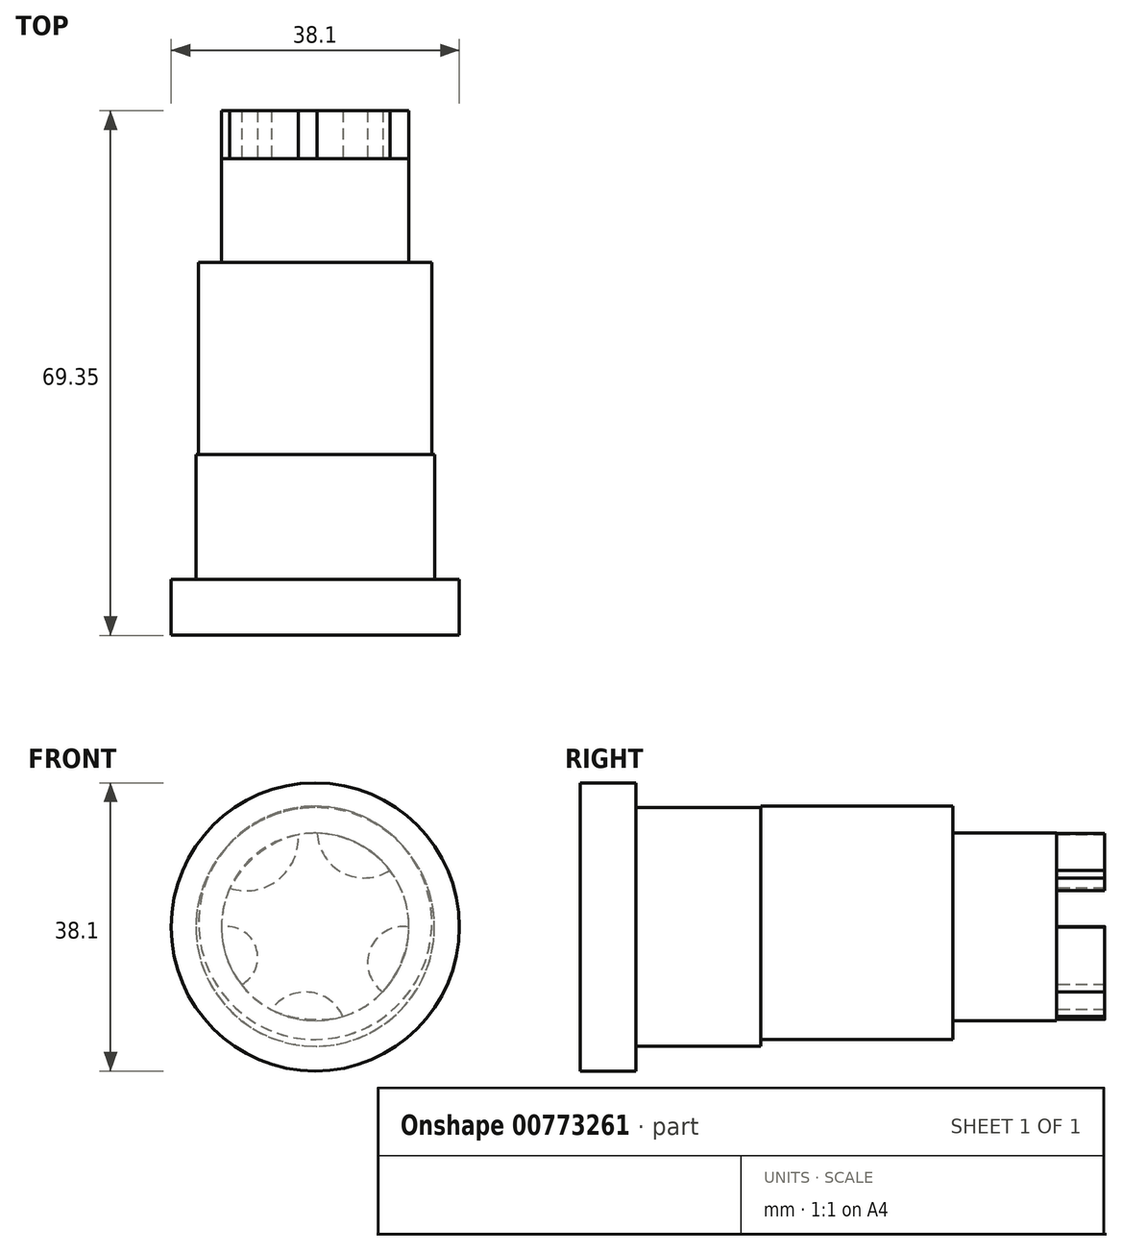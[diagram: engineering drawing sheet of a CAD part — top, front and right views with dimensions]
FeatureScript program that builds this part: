
annotation { "Feature Type Name" : "Feature", "Feature Type Description" : "" }
export const myFeature = defineFeature(function(context is Context, id is Id, definition is map)
    precondition{}
    {
        {
            var Q0;
            Q0=qCreatedBy(makeId("Front.planeOp"),FACE);
            var sketch = newSketch(context, id + "F0", { "sketchPlane" : qUnion([Q0])});
            skCircle(sketch, "E0", {"center": v(0, 0) * mm, "radius": 19.05 * mm});
            skSolve(sketch);
        }
        {
            var Q0;
            Q0 = qSketchRegion(id + "F0", true);
            extrude(context, id + "F1", {"entities" : qUnion([Q0]), "depth" : 7.37 * mm, "offsetDistance" : 25.4 * mm});
        }
        {
            var Q0;
            Q0=makeQuery(id+"F1.opExtrude","CAP_FACE",FACE,{"disambiguationData":[OSD([sQuery(id+"F0.wireOp",EDGE,"E0")])],"isStart":true});
            var sketch = newSketch(context, id + "F2", { "sketchPlane" : qUnion([Q0])});
            skCircle(sketch, "E1", {"center": v(0, 0) * mm, "radius": 15.77 * mm});
            skSolve(sketch);
        }
        {
            var Q0;
            Q0 = qSketchRegion(id + "F2", true);
            extrude(context, id + "F3", {"entities" : qUnion([Q0]), "operationType" : NewBodyOperationType.ADD, "depth" : 16.5 * mm, "offsetDistance" : 25.4 * mm});
        }
        {
            var Q0;
            Q0=makeQuery(id+"F3.opExtrude","CAP_FACE",FACE,{"disambiguationData":[OSD([sQuery(id+"F2.wireOp",EDGE,"E1")])],"isStart":false});
            var sketch = newSketch(context, id + "F4", { "sketchPlane" : qUnion([Q0])});
            skCircle(sketch, "E2", {"center": v(0, 0.54) * mm, "radius": 15.42 * mm});
            skSolve(sketch);
        }
        {
            var Q0;
            Q0 = qSketchRegion(id + "F4", true);
            extrude(context, id + "F5", {"entities" : qUnion([Q0]), "operationType" : NewBodyOperationType.ADD, "depth" : 25.4 * mm, "offsetDistance" : 25.4 * mm});
        }
        {
            var Q0;
            Q0=makeQuery(id+"F5.opExtrude","CAP_FACE",FACE,{"disambiguationData":[OSD([sQuery(id+"F4.wireOp",EDGE,"E2")])],"isStart":false});
            var sketch = newSketch(context, id + "F6", { "sketchPlane" : qUnion([Q0])});
            skCircle(sketch, "E3", {"center": v(0, 0) * mm, "radius": 10.8 * mm});
            skSolve(sketch);
        }
        {
            var Q0;
            Q0=makeQuery(id+"F6.imprint","IMPRINT",FACE,{"disambiguationData":[TD([[makeQuery(id+"F6.imprint","IMPRINT",EDGE,{"derivedFrom":sQuery(id+"F6.wireOp",EDGE,"E3")}),-1.0]])]});
            var sketch = newSketch(context, id + "F7", { "sketchPlane" : qUnion([Q0])});
            skCircle(sketch, "E4", {"center": v(0, 0) * mm, "radius": 12.4 * mm});
            skSolve(sketch);
        }
        {
            var Q0;
            Q0 = qSketchRegion(id + "F7", true);
            extrude(context, id + "F8", {"entities" : qUnion([Q0]), "operationType" : NewBodyOperationType.ADD, "depth" : 13.72 * mm, "offsetDistance" : 25.4 * mm});
        }
        {
            var Q0;
            Q0=makeQuery(id+"F8.opExtrude","CAP_FACE",FACE,{"disambiguationData":[OSD([sQuery(id+"F7.wireOp",EDGE,"E4")])],"isStart":false});
            var sketch = newSketch(context, id + "F9", { "sketchPlane" : qUnion([Q0])});
            skArc(sketch, "E5", {"start": v(-3.67, -11.83) * mm, "mid": v(1.14, -12.17) * mm, "end": v(5.81, -10.94) * mm});
            skArc(sketch, "E6", {"start": v(9.76, -7.63) * mm, "mid": v(11.73, -4.04) * mm, "end": v(12.4, 0) * mm});
            skArc(sketch, "E7", {"start": v(11.28, 5.12) * mm, "mid": v(7.56, 9.65) * mm, "end": v(2.27, 12.18) * mm});
            skArc(sketch, "E8", {"start": v(-12.4, 0) * mm, "mid": v(-11.43, -4.6) * mm, "end": v(-8.93, -8.59) * mm});
            skArc(sketch, "E9", {"start": v(-0.24, 12.39) * mm, "mid": v(-5.6, 11) * mm, "end": v(-9.88, 7.48) * mm});
            skArc(sketch, "E10", {"start": v(5.81, -10.94) * mm, "mid": v(0.81, -8.64) * mm, "end": v(-3.67, -11.83) * mm});
            skArc(sketch, "E11", {"start": v(12.4, 0) * mm, "mid": v(7.83, -2.7) * mm, "end": v(9.76, -7.63) * mm});
            skArc(sketch, "E12", {"start": v(2.27, 12.18) * mm, "mid": v(4.9, 6.25) * mm, "end": v(11.28, 5.12) * mm});
            skArc(sketch, "E13", {"start": v(-9.88, 7.48) * mm, "mid": v(-3.65, 7.16) * mm, "end": v(-0.24, 12.39) * mm});
            skArc(sketch, "E14", {"start": v(-8.93, -8.59) * mm, "mid": v(-7.28, -2.93) * mm, "end": v(-12.4, 0) * mm});
            skSolve(sketch);
        }
        {
            var Q0;
            Q0 = qSketchRegion(id + "F9", true);
            extrude(context, id + "F10", {"entities" : qUnion([Q0]), "operationType" : NewBodyOperationType.ADD, "depth" : 6.35 * mm, "offsetDistance" : 25.4 * mm});
        }
    });
